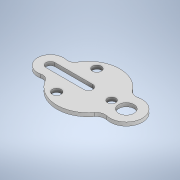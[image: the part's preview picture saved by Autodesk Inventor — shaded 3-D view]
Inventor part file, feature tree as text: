
AUTODESK INVENTOR PART (.ipt)
format: ipt  version: 2021 (Build 250183000, 183)  size: 151,040 bytes
history: native  units: mm
features: extrude x1, sketch x1
ambient origin geometry x8: Origin, YZ Plane, XZ Plane, XY Plane, X Axis, Y Axis, Z Axis, Center Point
bodies: Solid1 (feature_tree)
feature tree (2):
  extrude  "Extrusion1"  Depth=106.0mm
  sketch  "Sketch1"  dims[d1=72.0mm d2=106.0mm d3=40.0mm d4=0.0mm d5=40.0mm d7=90.0mm d8=212.0mm d9=50.0mm d10=50.0mm d11=0.0mm d12=130.0mm d13=23.0mm d14=43.0mm d15=25.0mm d16=25.0mm d18=120.0deg d19=120.0deg d20=25.0mm d21=25.0mm d22=10.0mm d23=0.0mm d24=0.5mm d25=0.872665mm]
